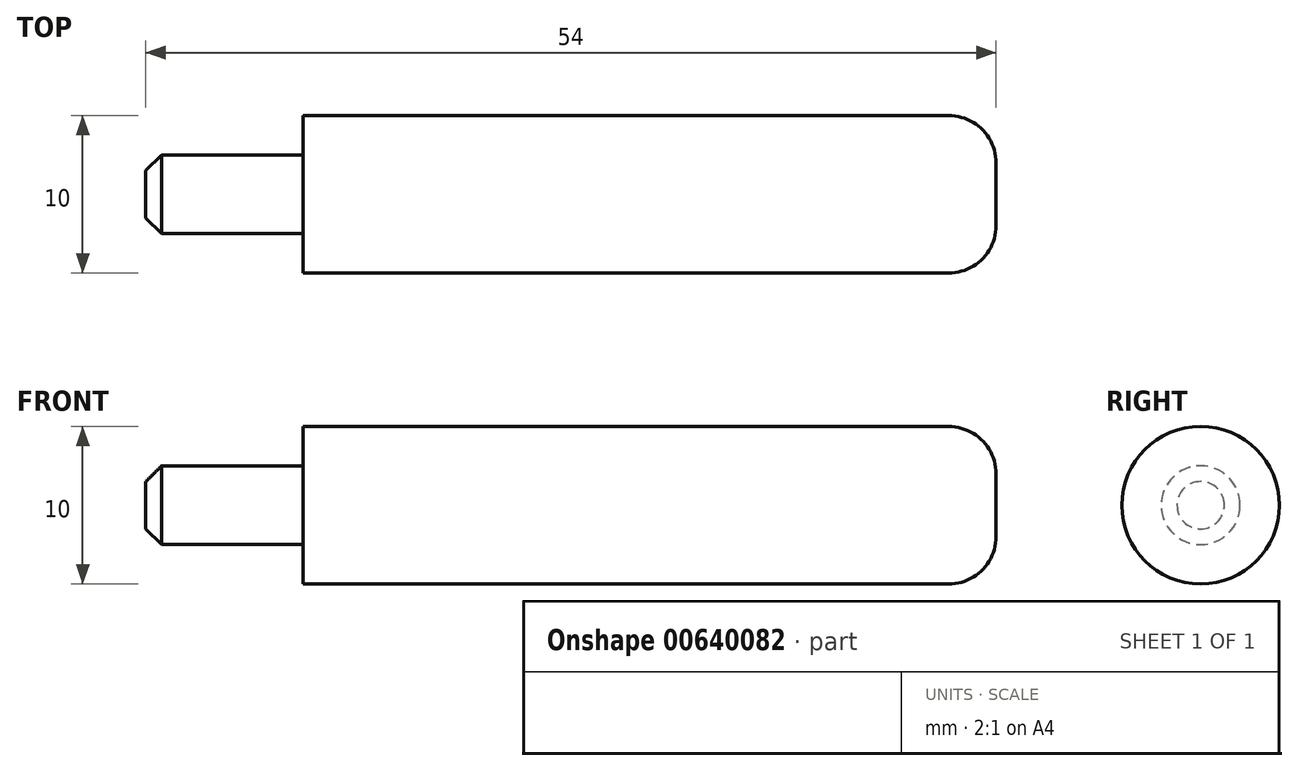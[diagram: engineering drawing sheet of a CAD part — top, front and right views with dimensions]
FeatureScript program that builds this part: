
annotation { "Feature Type Name" : "Feature", "Feature Type Description" : "" }
export const myFeature = defineFeature(function(context is Context, id is Id, definition is map)
    precondition{}
    {
        {
            var Q0;
            Q0=qCreatedBy(makeId("Right.planeOp"),FACE);
            var sketch = newSketch(context, id + "F0", { "sketchPlane" : qUnion([Q0])});
            skCircle(sketch, "E0", {"center": v(0, 0) * mm, "radius": 5 * mm});
            skSolve(sketch);
        }
        {
            var Q0;
            Q0 = qSketchRegion(id + "F0", true);
            extrude(context, id + "F1", {"entities" : qUnion([Q0]), "depth" : 44 * mm, "offsetDistance" : 25 * mm});
        }
        {
            var Q0;
            Q0=makeQuery(id+"F1.opExtrude","CAP_FACE",FACE,{"disambiguationData":[OSD([sQuery(id+"F0.wireOp",EDGE,"E0")])],"isStart":true});
            var sketch = newSketch(context, id + "F2", { "sketchPlane" : qUnion([Q0])});
            skCircle(sketch, "E1", {"center": v(0, 0) * mm, "radius": 2.5 * mm});
            skSolve(sketch);
        }
        {
            var Q0;
            Q0 = qSketchRegion(id + "F2", true);
            extrude(context, id + "F3", {"entities" : qUnion([Q0]), "operationType" : NewBodyOperationType.ADD, "depth" : 10 * mm, "offsetDistance" : 25 * mm});
        }
        {
            var Q0;
            Q0=makeQuery(id+"F3.opExtrude","CAP_EDGE",EDGE,{"disambiguationData":[OSD([sQuery(id+"F2.wireOp",EDGE,"E1")])],"isStart":false});
            chamfer(context, id + "F4", {"entities" : qUnion([Q0]), "width" : 1 * mm, "tangentPropagation" : true});
        }
        {
            var Q0;
            Q0=makeQuery(id+"F1.opExtrude","CAP_EDGE",EDGE,{"disambiguationData":[OSD([sQuery(id+"F0.wireOp",EDGE,"E0")])],"isStart":false});
            fillet(context, id + "F5", {"entities" : qUnion([Q0]), "radius" : 3 * mm, "tangentPropagation" : true, "allowEdgeOverflow" : false});
        }
    });
